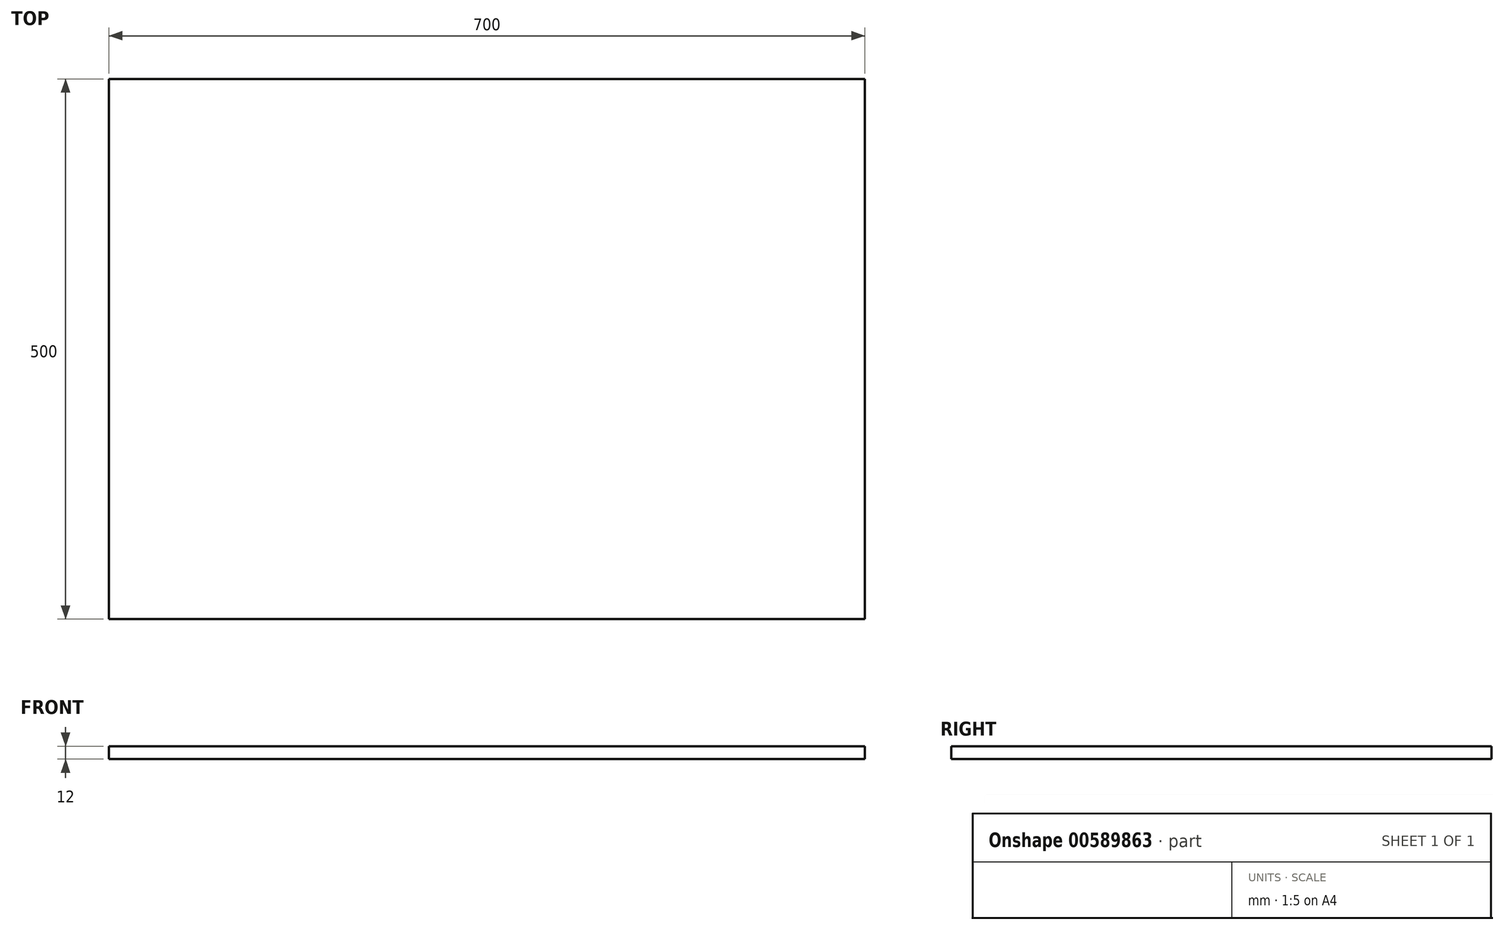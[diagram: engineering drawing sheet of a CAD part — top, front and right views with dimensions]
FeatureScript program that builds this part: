
annotation { "Feature Type Name" : "Feature", "Feature Type Description" : "" }
export const myFeature = defineFeature(function(context is Context, id is Id, definition is map)
    precondition{}
    {
        {
            var Q0;
            Q0=qCreatedBy(makeId("Top.planeOp"),FACE);
            var sketch = newSketch(context, id + "F0", { "sketchPlane" : qUnion([Q0])});
            skLineSegment(sketch, "E0.bottom", {"start": v(350, -250) * mm, "end": v(-350, -250) * mm});
            skLineSegment(sketch, "E0.top", {"start": v(350, 250) * mm, "end": v(-350, 250) * mm});
            skLineSegment(sketch, "E0.left", {"start": v(350, -250) * mm, "end": v(350, 250) * mm});
            skLineSegment(sketch, "E0.right", {"start": v(-350, -250) * mm, "end": v(-350, 250) * mm});
            skPoint(sketch, "E0.middle", {"position": v(0, 0) * mm});
            skSolve(sketch);
        }
        {
            var Q0;
            Q0 = qSketchRegion(id + "F0", true);
            extrude(context, id + "F1", {"entities" : qUnion([Q0]), "depth" : 12 * mm, "offsetDistance" : 25 * mm});
        }
    });
